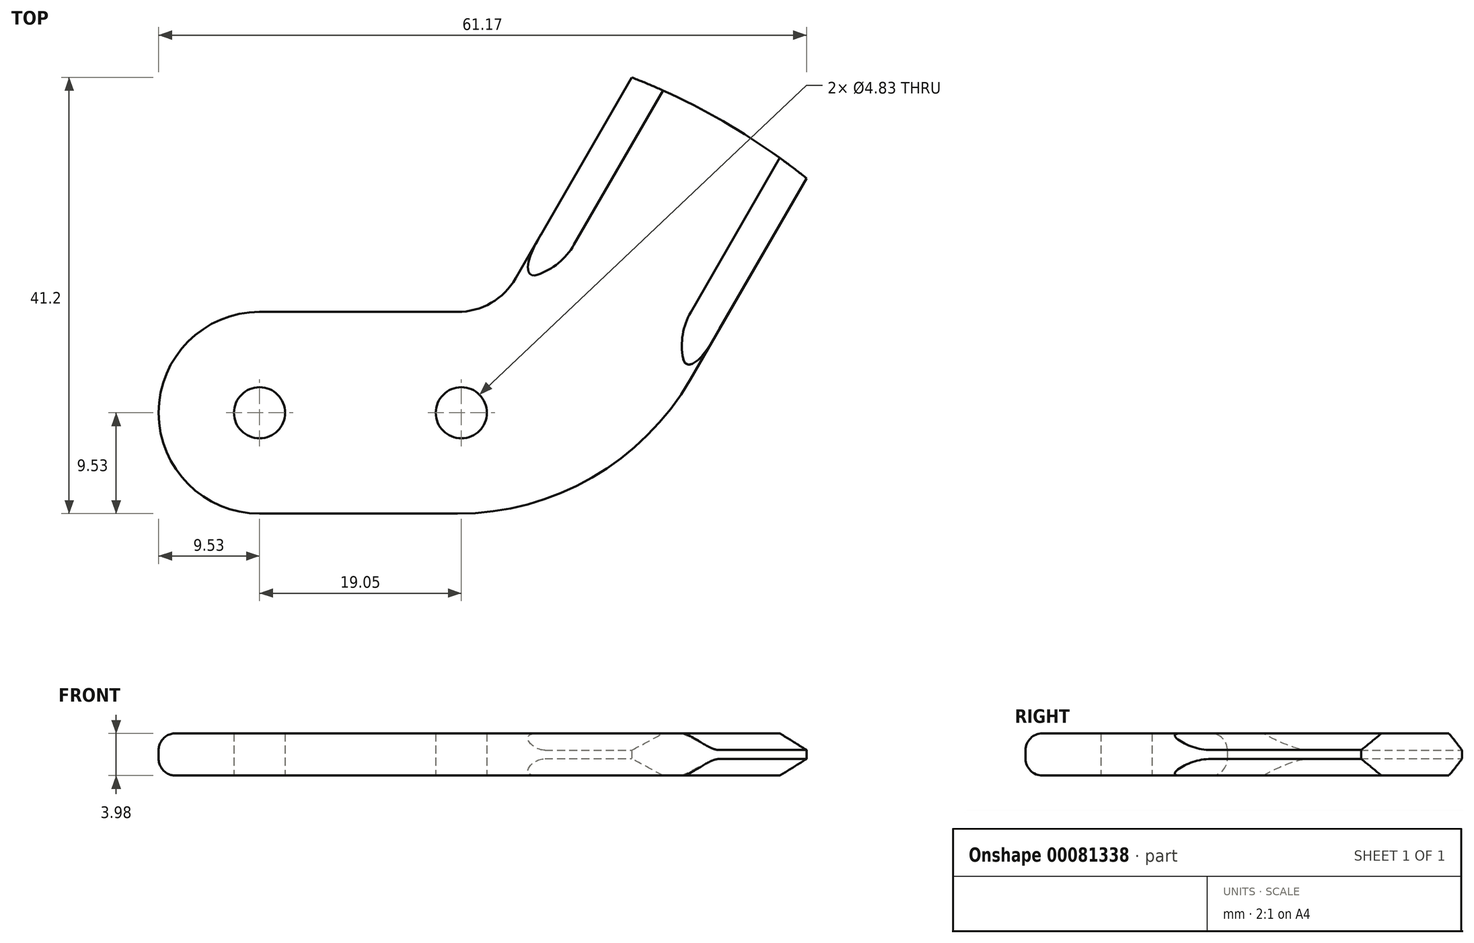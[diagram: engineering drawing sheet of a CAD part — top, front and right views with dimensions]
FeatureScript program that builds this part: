
annotation { "Feature Type Name" : "Feature", "Feature Type Description" : "" }
export const myFeature = defineFeature(function(context is Context, id is Id, definition is map)
    precondition{}
    {
        {
            var Q0;
            Q0=qCreatedBy(makeId("Top.planeOp"),FACE);
            var sketch = newSketch(context, id + "F0", { "sketchPlane" : qUnion([Q0])});
            skLineSegment(sketch, "E0", {"start": v(0, 9.53) * mm, "end": v(18.7, 9.53) * mm});
            skLineSegment(sketch, "E1", {"start": v(0, -9.53) * mm, "end": v(18.7, -9.53) * mm});
            skArc(sketch, "E2", {"start": v(0, 9.53) * mm, "mid": v(-9.53, 0) * mm, "end": v(0, -9.53) * mm});
            skCircle(sketch, "E3", {"center": v(0, 0) * mm, "radius": 2.41 * mm});
            skCircle(sketch, "E4", {"center": v(19.05, 0) * mm, "radius": 2.41 * mm});
            skLineSegment(sketch, "E5", {"start": v(-13.5, -31.75) * mm, "end": v(71.07, -31.75) * mm, "construction": true});
            skLineSegment(sketch, "E6", {"start": v(9.52, 27.08) * mm, "end": v(9.53, -31.75) * mm, "construction": true});
            skLineSegment(sketch, "E7", {"start": v(9.52, -31.75) * mm, "end": v(50.6, 39.4) * mm, "construction": true});
            skLineSegment(sketch, "E8.0", {"start": v(30.34, -14.75) * mm, "end": v(58.83, 34.6) * mm, "construction": true});
            skLineSegment(sketch, "E9.0", {"start": v(12.95, -6.77) * mm, "end": v(41.85, 43.28) * mm, "construction": true});
            skLineSegment(sketch, "E10", {"start": v(27.42, 36.96) * mm, "end": v(62.36, 16.79) * mm, "construction": true});
            skPoint(sketch, "E11", {"position": v(43.75, 27.53) * mm});
            skLineSegment(sketch, "E12", {"start": v(24.19, 12.7) * mm, "end": v(35.14, 31.67) * mm});
            skLineSegment(sketch, "E13", {"start": v(40.69, 3.17) * mm, "end": v(51.64, 22.15) * mm});
            skPoint(sketch, "E14.visualSharp", {"position": v(22.36, 9.53) * mm});
            skArc(sketch, "E14.filletArc", {"start": v(18.7, 9.52) * mm, "mid": v(21.87, 10.38) * mm, "end": v(24.19, 12.7) * mm});
            skPoint(sketch, "E15.visualSharp", {"position": v(33.36, -9.53) * mm});
            skArc(sketch, "E15.filletArc", {"start": v(18.7, -9.53) * mm, "mid": v(31.4, -6.12) * mm, "end": v(40.69, 3.18) * mm});
            skArc(sketch, "E16", {"start": v(51.64, 22.15) * mm, "mid": v(43.75, 27.53) * mm, "end": v(35.14, 31.67) * mm});
            skLineSegment(sketch, "E17.0", {"start": v(29.69, 15.88) * mm, "end": v(44.6, 41.7) * mm});
            skArc(sketch, "E18", {"start": v(24.19, 12.7) * mm, "mid": v(27.36, 13.55) * mm, "end": v(29.69, 15.87) * mm});
            skLineSegment(sketch, "E19.MirrorCS", {"start": v(40.69, 9.52) * mm, "end": v(55.6, 35.35) * mm});
            skArc(sketch, "E20.MirrorCS", {"start": v(40.69, 3.17) * mm, "mid": v(39.84, 6.35) * mm, "end": v(40.69, 9.52) * mm});
            skSolve(sketch);
        }
        {
            var Q0;
            Q0=makeQuery(id+"F0.imprint","IMPRINT",FACE,{"disambiguationData":[TD([[makeQuery(id+"F0.imprint","IMPRINT",EDGE,{"derivedFrom":sQuery(id+"F0.wireOp",EDGE,"E0")}),-1.0]])]});
            var Q1;
            {var subQ0=sQuery(id+"F0.wireOp",EDGE,"E12");Q1=makeQuery(id+"F0.imprint","IMPRINT",FACE,{"disambiguationData":[TD([[makeQuery(id+"F0.imprint","IMPRINT",EDGE,{"derivedFrom":subQ0}),-1.0]])]});}
            var Q2;
            {var subQ0=sQuery(id+"F0.wireOp",EDGE,"E13");Q2=makeQuery(id+"F0.imprint","IMPRINT",FACE,{"disambiguationData":[TD([[makeQuery(id+"F0.imprint","IMPRINT",EDGE,{"derivedFrom":subQ0}),1.0]])]});}
            extrude(context, id + "F1", {"entities" : qUnion([Q0, Q1, Q2]), "depth" : 4 * mm, "offsetDistance" : 25.4 * mm, "symmetric" : true});
        }
        {
            var Q0;
            Q0=sQuery(id+"F0.wireOp",EDGE,"E10");
            cPlane(context, id + "F2", {"entities" : qUnion([Q0]), "cplaneType" : CPlaneType.LINE_ANGLE, "offset" : 57 * mm, "angle" : 0 * degree, "oppositeDirection" : true, "width" : 152.4 * mm, "height" : 152.4 * mm});
        }
        {
            var Q0;
            Q0=qCreatedBy(id+"F2.planeOp",FACE);
            var sketch = newSketch(context, id + "F3", { "sketchPlane" : qUnion([Q0])});
            skLineSegment(sketch, "E21.0.0", {"start": v(-33.65, -2) * mm, "end": v(-14.6, -2) * mm});
            skLineSegment(sketch, "E21.0.1", {"start": v(-14.6, -2) * mm, "end": v(-14.6, 2) * mm});
            skLineSegment(sketch, "E21.0.2", {"start": v(-14.6, 2) * mm, "end": v(-33.65, 2) * mm});
            skLineSegment(sketch, "E21.0.3", {"start": v(-33.65, 2) * mm, "end": v(-33.65, -2) * mm});
            skLineSegment(sketch, "E22", {"start": v(-24.14, 0) * mm, "end": v(-24.14, 4.28) * mm, "construction": true});
            skLineSegment(sketch, "E23", {"start": v(-17.77, 2) * mm, "end": v(-14.6, 0.4) * mm});
            skLineSegment(sketch, "E24.MirrorCS", {"start": v(-30.5, 2) * mm, "end": v(-33.68, 0.4) * mm});
            skLineSegment(sketch, "E25.MirrorCS", {"start": v(-30.5, -2) * mm, "end": v(-33.68, -0.4) * mm});
            skLineSegment(sketch, "E26.MirrorCS", {"start": v(-17.77, -2) * mm, "end": v(-14.6, -0.4) * mm});
            skSolve(sketch);
        }
        {
            var Q0;
            Q0=makeQuery(id+"F1.opExtrude","CAP_EDGE",EDGE,{"disambiguationData":[OSD([sQuery(id+"F0.wireOp",EDGE,"E15.filletArc")])],"isStart":false});
            var Q1;
            Q1=makeQuery(id+"F1.opExtrude","CAP_EDGE",EDGE,{"disambiguationData":[OSD([sQuery(id+"F0.wireOp",EDGE,"E15.filletArc")])],"isStart":true});
            fillet(context, id + "F4", {"entities" : qUnion([Q0, Q1]), "radius" : 1.59 * mm, "tangentPropagation" : true, "allowEdgeOverflow" : false});
        }
        {
            var Q0;
            {var subQ3=sQuery(id+"F3.wireOp",EDGE,"E23");Q0=makeQuery(id+"F3.imprint","IMPRINT",FACE,{"disambiguationData":[TD([[makeQuery(id+"F3.imprint","IMPRINT",EDGE,{"derivedFrom":subQ3}),1.0]])]});}
            var Q1;
            {var subQ3=sQuery(id+"F3.wireOp",EDGE,"E26.MirrorCS");Q1=makeQuery(id+"F3.imprint","IMPRINT",FACE,{"disambiguationData":[TD([[makeQuery(id+"F3.imprint","IMPRINT",EDGE,{"derivedFrom":subQ3}),-1.0]])]});}
            var Q2;
            Q2=sQuery(id+"F0.wireOp",EDGE,"E17.0");
            var Q3;
            Q3=sQuery(id+"F0.wireOp",EDGE,"E18");
            sweep(context, id + "F5", {"operationType" : NewBodyOperationType.REMOVE, "profiles" : qUnion([Q0, Q1]), "path" : qUnion([Q2, Q3])});
        }
        {
            var Q0;
            {var subQ0=sQuery(id+"F3.wireOp",EDGE,"E21.0.3");var subQ1=sQuery(id+"F3.wireOp",EDGE,"E21.0.2");var subQ2=makeQuery(id+"F3.imprint","INTERSECT",VERTEX,{"derivedFrom":[subQ1,subQ0]});Q0=makeQuery(id+"F3.imprint","IMPRINT",FACE,{"disambiguationData":[TD([[makeQuery(id+"F3.imprint","IMPRINT",EDGE,{"disambiguationData":[TD([[subQ2,1.0]])],"derivedFrom":subQ1}),1.0]])]});}
            var Q1;
            {var subQ0=sQuery(id+"F3.wireOp",EDGE,"E21.0.3");var subQ1=sQuery(id+"F3.wireOp",EDGE,"E21.0.0");var subQ2=makeQuery(id+"F3.imprint","INTERSECT",VERTEX,{"derivedFrom":[subQ1,subQ0]});Q1=makeQuery(id+"F3.imprint","IMPRINT",FACE,{"disambiguationData":[TD([[makeQuery(id+"F3.imprint","IMPRINT",EDGE,{"disambiguationData":[TD([[subQ2,-1.0]])],"derivedFrom":subQ1}),1.0]])]});}
            var Q2;
            Q2=sQuery(id+"F0.wireOp",EDGE,"E19.MirrorCS");
            var Q3;
            Q3=sQuery(id+"F0.wireOp",EDGE,"E20.MirrorCS");
            sweep(context, id + "F6", {"operationType" : NewBodyOperationType.REMOVE, "profiles" : qUnion([Q0, Q1]), "path" : qUnion([Q2, Q3])});
        }
    });
